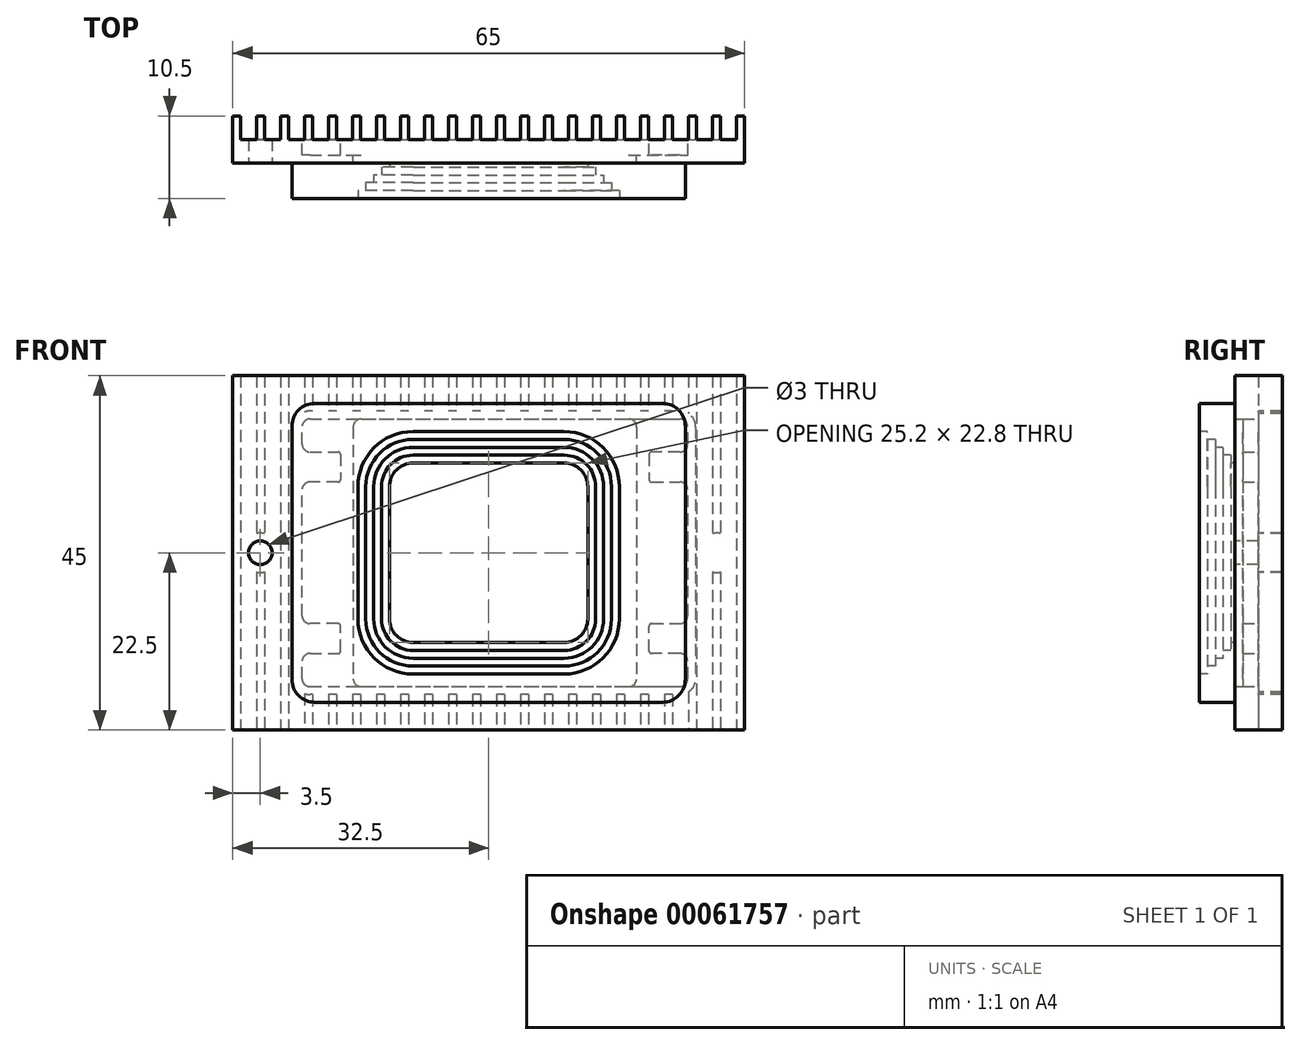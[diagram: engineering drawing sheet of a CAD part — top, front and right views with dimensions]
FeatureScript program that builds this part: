
annotation { "Feature Type Name" : "Feature", "Feature Type Description" : "" }
export const myFeature = defineFeature(function(context is Context, id is Id, definition is map)
    precondition{}
    {
        {
            var Q0;
            Q0=qCreatedBy(makeId("Front.planeOp"),FACE);
            var sketch = newSketch(context, id + "F0", { "sketchPlane" : qUnion([Q0])});
            skLineSegment(sketch, "E0.bottom", {"start": v(-32.5, 22.5) * mm, "end": v(32.5, 22.5) * mm});
            skLineSegment(sketch, "E0.top", {"start": v(-32.5, -22.5) * mm, "end": v(32.5, -22.5) * mm});
            skLineSegment(sketch, "E0.left", {"start": v(-32.5, 22.5) * mm, "end": v(-32.5, -22.5) * mm});
            skLineSegment(sketch, "E0.right", {"start": v(32.5, 22.5) * mm, "end": v(32.5, -22.5) * mm});
            skPoint(sketch, "E1.visualSharp", {"position": v(-32.5, 22.5) * mm});
            skLineSegment(sketch, "E1.filletArc", {"start": v(-32.5, 22.5) * mm, "end": v(-32.5, 22.5) * mm});
            skPoint(sketch, "E2.visualSharp", {"position": v(32.5, 22.5) * mm});
            skLineSegment(sketch, "E2.filletArc", {"start": v(32.5, 22.5) * mm, "end": v(32.5, 22.5) * mm});
            skPoint(sketch, "E3.visualSharp", {"position": v(32.5, -22.5) * mm});
            skLineSegment(sketch, "E3.filletArc", {"start": v(32.5, -22.5) * mm, "end": v(32.5, -22.5) * mm});
            skPoint(sketch, "E4.visualSharp", {"position": v(-32.5, -22.5) * mm});
            skLineSegment(sketch, "E4.filletArc", {"start": v(-32.5, -22.5) * mm, "end": v(-32.5, -22.5) * mm});
            skPoint(sketch, "E5", {"position": v(0, 22.5) * mm});
            skPoint(sketch, "E6", {"position": v(32.5, 0) * mm});
            skSolve(sketch);
        }
        {
            var Q0;
            Q0=makeQuery(id+"F0.imprint","IMPRINT",FACE,{"disambiguationData":[TD([[makeQuery(id+"F0.imprint","IMPRINT",EDGE,{"derivedFrom":sQuery(id+"F0.wireOp",EDGE,"E0.bottom")}),-1.0]])]});
            var Q1;
            Q1=makeQuery(id+"F0.imprint","IMPRINT",FACE,{"disambiguationData":[TD([[makeQuery(id+"F0.imprint","IMPRINT",EDGE,{"derivedFrom":sQuery(id+"F0.wireOp",EDGE,"E0.bottom")}),-1.0]])]});
            extrude(context, id + "F1", {"entities" : qUnion([Q0, Q1]), "depth" : 3 * mm});
        }
        {
            var Q0;
            Q0=makeQuery(id+"F1.opExtrude","CAP_FACE",FACE,{"disambiguationData":[OSD([sQuery(id+"F0.wireOp",EDGE,"E0.bottom"),sQuery(id+"F0.wireOp",EDGE,"E0.top"),sQuery(id+"F0.wireOp",EDGE,"E0.left"),sQuery(id+"F0.wireOp",EDGE,"E0.right"),sQuery(id+"F0.wireOp",EDGE,"E1.filletArc"),sQuery(id+"F0.wireOp",EDGE,"E2.filletArc"),sQuery(id+"F0.wireOp",EDGE,"E3.filletArc"),sQuery(id+"F0.wireOp",EDGE,"E4.filletArc")])],"isStart":false});
            var sketch = newSketch(context, id + "F2", { "sketchPlane" : qUnion([Q0])});
            skLineSegment(sketch, "E7.bottom", {"start": v(-22.09, 18.99) * mm, "end": v(22.09, 18.99) * mm});
            skLineSegment(sketch, "E7.top", {"start": v(-22.09, -18.99) * mm, "end": v(22.09, -18.99) * mm});
            skLineSegment(sketch, "E7.left", {"start": v(-24.98, 16.09) * mm, "end": v(-24.98, -16.09) * mm});
            skLineSegment(sketch, "E7.right", {"start": v(24.98, 16.09) * mm, "end": v(24.98, -16.09) * mm});
            skPoint(sketch, "E8", {"position": v(0, 18.99) * mm});
            skPoint(sketch, "E9", {"position": v(24.98, 0) * mm});
            skPoint(sketch, "E10.visualSharp", {"position": v(-24.98, 18.99) * mm});
            skArc(sketch, "E10.filletArc", {"start": v(-22.09, 18.99) * mm, "mid": v(-24.14, 18.14) * mm, "end": v(-24.98, 16.09) * mm});
            skPoint(sketch, "E11.visualSharp", {"position": v(24.99, -18.98) * mm});
            skArc(sketch, "E11.filletArc", {"start": v(22.09, -18.99) * mm, "mid": v(24.14, -18.14) * mm, "end": v(24.98, -16.09) * mm});
            skPoint(sketch, "E12.visualSharp", {"position": v(24.99, 18.98) * mm});
            skArc(sketch, "E12.filletArc", {"start": v(24.98, 16.09) * mm, "mid": v(24.14, 18.14) * mm, "end": v(22.09, 18.99) * mm});
            skPoint(sketch, "E13.visualSharp", {"position": v(-24.98, -18.99) * mm});
            skArc(sketch, "E13.filletArc", {"start": v(-24.98, -16.09) * mm, "mid": v(-24.14, -18.14) * mm, "end": v(-22.09, -18.99) * mm});
            skSolve(sketch);
        }
        {
            var Q0;
            Q0=makeQuery(id+"F2.imprint","IMPRINT",FACE,{"disambiguationData":[TD([[makeQuery(id+"F2.imprint","IMPRINT",EDGE,{"derivedFrom":sQuery(id+"F2.wireOp",EDGE,"E7.bottom")}),-1.0]])]});
            extrude(context, id + "F3", {"entities" : qUnion([Q0]), "operationType" : NewBodyOperationType.ADD, "depth" : 4.5 * mm});
        }
        {
            var Q0;
            Q0=makeQuery(id+"F3.opExtrude","CAP_FACE",FACE,{"disambiguationData":[OSD([sQuery(id+"F2.wireOp",EDGE,"E7.bottom"),sQuery(id+"F2.wireOp",EDGE,"E7.top"),sQuery(id+"F2.wireOp",EDGE,"E7.left"),sQuery(id+"F2.wireOp",EDGE,"E7.right"),sQuery(id+"F2.wireOp",EDGE,"E10.filletArc"),sQuery(id+"F2.wireOp",EDGE,"E11.filletArc"),sQuery(id+"F2.wireOp",EDGE,"E12.filletArc"),sQuery(id+"F2.wireOp",EDGE,"E13.filletArc")])],"isStart":false});
            var sketch = newSketch(context, id + "F4", { "sketchPlane" : qUnion([Q0])});
            skLineSegment(sketch, "E14.bottom", {"start": v(-9.6, 11.4) * mm, "end": v(9.6, 11.4) * mm});
            skLineSegment(sketch, "E14.top", {"start": v(-9.6, -11.4) * mm, "end": v(9.6, -11.4) * mm});
            skLineSegment(sketch, "E14.left", {"start": v(-12.6, 8.4) * mm, "end": v(-12.6, -8.4) * mm});
            skLineSegment(sketch, "E14.right", {"start": v(12.6, 8.4) * mm, "end": v(12.6, -8.4) * mm});
            skPoint(sketch, "E15", {"position": v(0, 11.4) * mm});
            skPoint(sketch, "E16", {"position": v(12.6, 0) * mm});
            skPoint(sketch, "E17.visualSharp", {"position": v(-12.6, 11.4) * mm});
            skArc(sketch, "E17.filletArc", {"start": v(-9.6, 11.4) * mm, "mid": v(-11.72, 10.52) * mm, "end": v(-12.6, 8.4) * mm});
            skPoint(sketch, "E18.visualSharp", {"position": v(12.6, 11.4) * mm});
            skArc(sketch, "E18.filletArc", {"start": v(12.6, 8.4) * mm, "mid": v(11.72, 10.52) * mm, "end": v(9.6, 11.4) * mm});
            skPoint(sketch, "E19.visualSharp", {"position": v(12.6, -11.4) * mm});
            skArc(sketch, "E19.filletArc", {"start": v(9.6, -11.4) * mm, "mid": v(11.72, -10.52) * mm, "end": v(12.6, -8.4) * mm});
            skPoint(sketch, "E20.visualSharp", {"position": v(-12.6, -11.4) * mm});
            skArc(sketch, "E20.filletArc", {"start": v(-12.6, -8.4) * mm, "mid": v(-11.72, -10.52) * mm, "end": v(-9.6, -11.4) * mm});
            skCircle(sketch, "E21", {"center": v(-29, 0) * mm, "radius": 1.5 * mm});
            skCircle(sketch, "E22.MirrorC", {"center": v(29, 0) * mm, "radius": 1.5 * mm});
            skSolve(sketch);
        }
        {
            var Q0;
            Q0=makeQuery(id+"F4.imprint","IMPRINT",FACE,{"disambiguationData":[TD([[makeQuery(id+"F4.imprint","IMPRINT",EDGE,{"derivedFrom":sQuery(id+"F4.wireOp",EDGE,"E14.bottom")}),-1.0]])]});
            var Q1;
            Q1=makeQuery(id+"F4.imprint","IMPRINT",FACE,{"disambiguationData":[TD([[makeQuery(id+"F4.imprint","IMPRINT",EDGE,{"derivedFrom":sQuery(id+"F4.wireOp",EDGE,"E21")}),1.0]])]});
            var Q2;
            Q2=makeQuery(id+"F4.imprint","IMPRINT",FACE,{"disambiguationData":[TD([[makeQuery(id+"F4.imprint","IMPRINT",EDGE,{"derivedFrom":sQuery(id+"F4.wireOp",EDGE,"E22.MirrorC")}),-1.0]])]});
            extrude(context, id + "F5", {"entities" : qUnion([Q0, Q1, Q2]), "operationType" : NewBodyOperationType.REMOVE, "oppositeDirection" : true, "depth" : 25 * mm});
        }
        {
            var Q0;
            Q0=makeQuery(id+"F1.opExtrude","CAP_FACE",FACE,{"disambiguationData":[OSD([sQuery(id+"F0.wireOp",EDGE,"E0.bottom"),sQuery(id+"F0.wireOp",EDGE,"E0.top"),sQuery(id+"F0.wireOp",EDGE,"E0.left"),sQuery(id+"F0.wireOp",EDGE,"E0.right")])],"isStart":true});
            var sketch = newSketch(context, id + "F6", { "sketchPlane" : qUnion([Q0])});
            skPoint(sketch, "E23", {"position": v(-32.5, 0) * mm});
            skPoint(sketch, "E23.positionSnap0", {"position": v(-25.3, 0) * mm});
            skLineSegment(sketch, "E24", {"start": v(-24.3, -12.8) * mm, "end": v(-20.7, -12.8) * mm});
            skLineSegment(sketch, "E25", {"start": v(-20.4, -12.5) * mm, "end": v(-20.4, -9.3) * mm});
            skLineSegment(sketch, "E26", {"start": v(-20.7, -9) * mm, "end": v(-24.3, -9) * mm});
            skLineSegment(sketch, "E27", {"start": v(-24.3, 12.8) * mm, "end": v(-20.7, 12.8) * mm});
            skLineSegment(sketch, "E28", {"start": v(-20.4, 12.5) * mm, "end": v(-20.4, 9.3) * mm});
            skLineSegment(sketch, "E29", {"start": v(-20.7, 9) * mm, "end": v(-24.3, 9) * mm});
            skLineSegment(sketch, "E30", {"start": v(-0.8, 17) * mm, "end": v(-0.8, -17) * mm, "construction": true});
            skLineSegment(sketch, "E31", {"start": v(-25.3, -16) * mm, "end": v(-25.3, -13.8) * mm});
            skLineSegment(sketch, "E32", {"start": v(-25.3, -8) * mm, "end": v(-25.3, 8) * mm});
            skLineSegment(sketch, "E33", {"start": v(-25.3, 13.8) * mm, "end": v(-25.3, 16) * mm});
            skPoint(sketch, "E34.visualSharp", {"position": v(-25.3, 12.8) * mm});
            skArc(sketch, "E34.filletArc", {"start": v(-25.3, 13.8) * mm, "mid": v(-25, 13.1) * mm, "end": v(-24.3, 12.8) * mm});
            skPoint(sketch, "E35.visualSharp", {"position": v(-25.3, 17.24) * mm});
            skArc(sketch, "E35.filletArc", {"start": v(-24.3, 17) * mm, "mid": v(-25, 16.7) * mm, "end": v(-25.3, 16) * mm});
            skPoint(sketch, "E36.visualSharp", {"position": v(-25.3, -9) * mm});
            skArc(sketch, "E36.filletArc", {"start": v(-25.3, -8) * mm, "mid": v(-25, -8.7) * mm, "end": v(-24.3, -9) * mm});
            skPoint(sketch, "E37.visualSharp", {"position": v(-25.3, -17.23) * mm});
            skArc(sketch, "E37.filletArc", {"start": v(-25.3, -16) * mm, "mid": v(-25, -16.7) * mm, "end": v(-24.3, -17) * mm});
            skPoint(sketch, "E38.visualSharp", {"position": v(-20.4, 9) * mm});
            skArc(sketch, "E38.filletArc", {"start": v(-20.7, 9) * mm, "mid": v(-20.49, 9.09) * mm, "end": v(-20.4, 9.3) * mm});
            skPoint(sketch, "E39.visualSharp", {"position": v(-20.4, 12.8) * mm});
            skArc(sketch, "E39.filletArc", {"start": v(-20.4, 12.5) * mm, "mid": v(-20.49, 12.71) * mm, "end": v(-20.7, 12.8) * mm});
            skPoint(sketch, "E40.visualSharp", {"position": v(-20.4, -9) * mm});
            skArc(sketch, "E40.filletArc", {"start": v(-20.4, -9.3) * mm, "mid": v(-20.49, -9.09) * mm, "end": v(-20.7, -9) * mm});
            skPoint(sketch, "E41.visualSharp", {"position": v(-20.4, -12.8) * mm});
            skArc(sketch, "E41.filletArc", {"start": v(-20.7, -12.8) * mm, "mid": v(-20.49, -12.71) * mm, "end": v(-20.4, -12.5) * mm});
            skPoint(sketch, "E42.visualSharp", {"position": v(-25.3, 9) * mm});
            skArc(sketch, "E42.filletArc", {"start": v(-24.3, 9) * mm, "mid": v(-25, 8.7) * mm, "end": v(-25.3, 8) * mm});
            skPoint(sketch, "E43.visualSharp", {"position": v(-25.3, -12.8) * mm});
            skArc(sketch, "E43.filletArc", {"start": v(-24.3, -12.8) * mm, "mid": v(-25, -13.1) * mm, "end": v(-25.3, -13.8) * mm});
            skArc(sketch, "E44.MirrorCS", {"start": v(23.7, -16) * mm, "mid": v(23.4, -16.7) * mm, "end": v(22.7, -17) * mm});
            skArc(sketch, "E45.MirrorCS", {"start": v(22.7, -12.8) * mm, "mid": v(23.4, -13.1) * mm, "end": v(23.7, -13.8) * mm});
            skLineSegment(sketch, "E46.MirrorCS", {"start": v(22.7, -12.8) * mm, "end": v(19.1, -12.8) * mm});
            skArc(sketch, "E47.MirrorCS", {"start": v(19.1, -12.8) * mm, "mid": v(18.89, -12.71) * mm, "end": v(18.8, -12.5) * mm});
            skLineSegment(sketch, "E48.MirrorCS", {"start": v(18.8, -12.5) * mm, "end": v(18.8, -9.3) * mm});
            skArc(sketch, "E49.MirrorCS", {"start": v(18.8, -9.3) * mm, "mid": v(18.89, -9.09) * mm, "end": v(19.1, -9) * mm});
            skLineSegment(sketch, "E50.MirrorCS", {"start": v(19.1, -9) * mm, "end": v(22.7, -9) * mm});
            skArc(sketch, "E51.MirrorCS", {"start": v(23.7, -8) * mm, "mid": v(23.4, -8.7) * mm, "end": v(22.7, -9) * mm});
            skLineSegment(sketch, "E52.MirrorCS", {"start": v(23.7, -8) * mm, "end": v(23.7, 8) * mm});
            skArc(sketch, "E53.MirrorCS", {"start": v(22.7, 9) * mm, "mid": v(23.4, 8.7) * mm, "end": v(23.7, 8) * mm});
            skLineSegment(sketch, "E54.MirrorCS", {"start": v(19.1, 9) * mm, "end": v(22.7, 9) * mm});
            skArc(sketch, "E55.MirrorCS", {"start": v(19.1, 9) * mm, "mid": v(18.89, 9.09) * mm, "end": v(18.8, 9.3) * mm});
            skLineSegment(sketch, "E56.MirrorCS", {"start": v(18.8, 12.5) * mm, "end": v(18.8, 9.3) * mm});
            skArc(sketch, "E57.MirrorCS", {"start": v(18.8, 12.5) * mm, "mid": v(18.89, 12.71) * mm, "end": v(19.1, 12.8) * mm});
            skLineSegment(sketch, "E58.MirrorCS", {"start": v(22.7, 12.8) * mm, "end": v(19.1, 12.8) * mm});
            skArc(sketch, "E59.MirrorCS", {"start": v(23.7, 13.8) * mm, "mid": v(23.4, 13.1) * mm, "end": v(22.7, 12.8) * mm});
            skLineSegment(sketch, "E60.MirrorCS", {"start": v(23.7, 13.8) * mm, "end": v(23.7, 16) * mm});
            skArc(sketch, "E61.MirrorCS", {"start": v(22.7, 17) * mm, "mid": v(23.4, 16.7) * mm, "end": v(23.7, 16) * mm});
            skLineSegment(sketch, "E62", {"start": v(22.7, -17) * mm, "end": v(-24.3, -17) * mm});
            skLineSegment(sketch, "E63", {"start": v(22.7, 17) * mm, "end": v(-24.3, 17) * mm});
            skLineSegment(sketch, "E64", {"start": v(-25.3, 0) * mm, "end": v(23.7, 0) * mm, "construction": true});
            skLineSegment(sketch, "E65.MirrorCS", {"start": v(23.7, -16) * mm, "end": v(23.7, -13.8) * mm});
            skLineSegment(sketch, "E66.bottom", {"start": v(-24.3, 16.9) * mm, "end": v(22.7, 16.9) * mm, "construction": true});
            skLineSegment(sketch, "E66.top", {"start": v(-24.3, -16.9) * mm, "end": v(22.7, -16.9) * mm, "construction": true});
            skLineSegment(sketch, "E66.left", {"start": v(-24.3, 16.9) * mm, "end": v(-24.3, -16.9) * mm, "construction": true});
            skLineSegment(sketch, "E66.right", {"start": v(22.7, 16.9) * mm, "end": v(22.7, -16.9) * mm, "construction": true});
            skLineSegment(sketch, "E67", {"start": v(-24.3, -16.9) * mm, "end": v(22.7, 16.9) * mm, "construction": true});
            skLineSegment(sketch, "E68", {"start": v(22.7, -16.9) * mm, "end": v(-24.3, 16.9) * mm, "construction": true});
            skPoint(sketch, "E69", {"position": v(-0.8, 0) * mm});
            skLineSegment(sketch, "E70.bottom", {"start": v(22.7, 12.9) * mm, "end": v(18.7, 12.9) * mm, "construction": true});
            skLineSegment(sketch, "E70.top", {"start": v(22.7, 8.9) * mm, "end": v(18.7, 8.9) * mm, "construction": true});
            skLineSegment(sketch, "E70.left", {"start": v(22.7, 12.9) * mm, "end": v(22.7, 8.9) * mm, "construction": true});
            skLineSegment(sketch, "E70.right", {"start": v(18.7, 12.9) * mm, "end": v(18.7, 8.9) * mm, "construction": true});
            skSolve(sketch);
        }
        {
            var Q0;
            Q0=makeQuery(id+"F6.imprint","IMPRINT",FACE,{"disambiguationData":[TD([[makeQuery(id+"F6.imprint","IMPRINT",EDGE,{"derivedFrom":sQuery(id+"F6.wireOp",EDGE,"E24")}),-1.0]])]});
            extrude(context, id + "F7", {"entities" : qUnion([Q0]), "operationType" : NewBodyOperationType.REMOVE, "oppositeDirection" : true, "depth" : 2 * mm});
        }
        {
            var Q0;
            Q0=makeQuery(id+"F3.opExtrude","CAP_FACE",FACE,{"disambiguationData":[OSD([sQuery(id+"F2.wireOp",EDGE,"E7.bottom"),sQuery(id+"F2.wireOp",EDGE,"E7.top"),sQuery(id+"F2.wireOp",EDGE,"E7.left"),sQuery(id+"F2.wireOp",EDGE,"E7.right"),sQuery(id+"F2.wireOp",EDGE,"E10.filletArc"),sQuery(id+"F2.wireOp",EDGE,"E11.filletArc"),sQuery(id+"F2.wireOp",EDGE,"E12.filletArc"),sQuery(id+"F2.wireOp",EDGE,"E13.filletArc")])],"isStart":false});
            var sketch = newSketch(context, id + "F8", { "sketchPlane" : qUnion([Q0])});
            skLineSegment(sketch, "E71.0", {"start": v(-9.6, 12.4) * mm, "end": v(9.6, 12.4) * mm});
            skArc(sketch, "E71.1", {"start": v(13.6, 8.4) * mm, "mid": v(12.43, 11.23) * mm, "end": v(9.6, 12.4) * mm});
            skArc(sketch, "E71.2", {"start": v(-9.6, 12.4) * mm, "mid": v(-12.43, 11.23) * mm, "end": v(-13.6, 8.4) * mm});
            skLineSegment(sketch, "E71.3", {"start": v(13.6, 8.4) * mm, "end": v(13.6, -8.4) * mm});
            skLineSegment(sketch, "E71.4", {"start": v(-13.6, 8.4) * mm, "end": v(-13.6, -8.4) * mm});
            skArc(sketch, "E71.5", {"start": v(-13.6, -8.4) * mm, "mid": v(-12.43, -11.23) * mm, "end": v(-9.6, -12.4) * mm});
            skLineSegment(sketch, "E71.6", {"start": v(-9.6, -12.4) * mm, "end": v(9.6, -12.4) * mm});
            skArc(sketch, "E71.7", {"start": v(9.6, -12.4) * mm, "mid": v(12.43, -11.23) * mm, "end": v(13.6, -8.4) * mm});
            skSolve(sketch);
        }
        {
            var Q0;
            Q0=makeQuery(id+"F8.imprint","IMPRINT",FACE,{"disambiguationData":[TD([[makeQuery(id+"F8.imprint","IMPRINT",EDGE,{"derivedFrom":sQuery(id+"F8.wireOp",EDGE,"E71.0")}),-1.0]])]});
            extrude(context, id + "F9", {"entities" : qUnion([Q0]), "operationType" : NewBodyOperationType.REMOVE, "oppositeDirection" : true, "depth" : 4 * mm});
        }
        {
            var Q0;
            Q0=makeQuery(id+"F3.opExtrude","CAP_FACE",FACE,{"disambiguationData":[OSD([sQuery(id+"F2.wireOp",EDGE,"E7.bottom"),sQuery(id+"F2.wireOp",EDGE,"E7.top"),sQuery(id+"F2.wireOp",EDGE,"E7.left"),sQuery(id+"F2.wireOp",EDGE,"E7.right"),sQuery(id+"F2.wireOp",EDGE,"E10.filletArc"),sQuery(id+"F2.wireOp",EDGE,"E11.filletArc"),sQuery(id+"F2.wireOp",EDGE,"E12.filletArc"),sQuery(id+"F2.wireOp",EDGE,"E13.filletArc")])],"isStart":false});
            var sketch = newSketch(context, id + "F10", { "sketchPlane" : qUnion([Q0])});
            skLineSegment(sketch, "E72.0", {"start": v(-9.6, 13.4) * mm, "end": v(9.6, 13.4) * mm});
            skArc(sketch, "E72.1", {"start": v(14.6, 8.4) * mm, "mid": v(13.14, 11.94) * mm, "end": v(9.6, 13.4) * mm});
            skArc(sketch, "E72.2", {"start": v(-9.6, 13.4) * mm, "mid": v(-13.14, 11.94) * mm, "end": v(-14.6, 8.4) * mm});
            skLineSegment(sketch, "E72.3", {"start": v(14.6, 8.4) * mm, "end": v(14.6, -8.4) * mm});
            skLineSegment(sketch, "E72.4", {"start": v(-14.6, 8.4) * mm, "end": v(-14.6, -8.4) * mm});
            skArc(sketch, "E72.5", {"start": v(-14.6, -8.4) * mm, "mid": v(-13.14, -11.94) * mm, "end": v(-9.6, -13.4) * mm});
            skLineSegment(sketch, "E72.6", {"start": v(-9.6, -13.4) * mm, "end": v(9.6, -13.4) * mm});
            skArc(sketch, "E72.7", {"start": v(9.6, -13.4) * mm, "mid": v(13.14, -11.94) * mm, "end": v(14.6, -8.4) * mm});
            skLineSegment(sketch, "E73.0", {"start": v(19.98, 13.99) * mm, "end": v(-19.98, 13.99) * mm});
            skLineSegment(sketch, "E73.1", {"start": v(19.98, -13.99) * mm, "end": v(19.98, 13.99) * mm});
            skLineSegment(sketch, "E73.2", {"start": v(-19.98, -13.99) * mm, "end": v(19.98, -13.99) * mm});
            skLineSegment(sketch, "E73.3", {"start": v(-19.98, 13.99) * mm, "end": v(-19.98, -13.99) * mm});
            skSolve(sketch);
        }
        {
            var Q0;
            Q0=makeQuery(id+"F10.imprint","IMPRINT",FACE,{"disambiguationData":[TD([[makeQuery(id+"F10.imprint","IMPRINT",EDGE,{"derivedFrom":sQuery(id+"F10.wireOp",EDGE,"E72.0")}),-1.0]])]});
            extrude(context, id + "F11", {"entities" : qUnion([Q0]), "operationType" : NewBodyOperationType.REMOVE, "oppositeDirection" : true, "depth" : 3 * mm});
        }
        {
            var Q0;
            Q0=makeQuery(id+"F3.opExtrude","CAP_FACE",FACE,{"disambiguationData":[OSD([sQuery(id+"F2.wireOp",EDGE,"E7.bottom"),sQuery(id+"F2.wireOp",EDGE,"E7.top"),sQuery(id+"F2.wireOp",EDGE,"E7.left"),sQuery(id+"F2.wireOp",EDGE,"E7.right"),sQuery(id+"F2.wireOp",EDGE,"E10.filletArc"),sQuery(id+"F2.wireOp",EDGE,"E11.filletArc"),sQuery(id+"F2.wireOp",EDGE,"E12.filletArc"),sQuery(id+"F2.wireOp",EDGE,"E13.filletArc")])],"isStart":false});
            var sketch = newSketch(context, id + "F12", { "sketchPlane" : qUnion([Q0])});
            skLineSegment(sketch, "E74.0", {"start": v(-9.6, 14.4) * mm, "end": v(9.6, 14.4) * mm});
            skArc(sketch, "E74.1", {"start": v(15.6, 8.4) * mm, "mid": v(13.84, 12.64) * mm, "end": v(9.6, 14.4) * mm});
            skArc(sketch, "E74.2", {"start": v(-9.6, 14.4) * mm, "mid": v(-13.84, 12.64) * mm, "end": v(-15.6, 8.4) * mm});
            skLineSegment(sketch, "E74.3", {"start": v(15.6, 8.4) * mm, "end": v(15.6, -8.4) * mm});
            skLineSegment(sketch, "E74.4", {"start": v(-15.6, 8.4) * mm, "end": v(-15.6, -8.4) * mm});
            skArc(sketch, "E74.5", {"start": v(-15.6, -8.4) * mm, "mid": v(-13.84, -12.64) * mm, "end": v(-9.6, -14.4) * mm});
            skLineSegment(sketch, "E74.6", {"start": v(-9.6, -14.4) * mm, "end": v(9.6, -14.4) * mm});
            skArc(sketch, "E74.7", {"start": v(9.6, -14.4) * mm, "mid": v(13.84, -12.64) * mm, "end": v(15.6, -8.4) * mm});
            skSolve(sketch);
        }
        {
            var Q0;
            Q0=makeQuery(id+"F12.imprint","IMPRINT",FACE,{"disambiguationData":[TD([[makeQuery(id+"F12.imprint","IMPRINT",EDGE,{"derivedFrom":sQuery(id+"F12.wireOp",EDGE,"E74.0")}),-1.0]])]});
            extrude(context, id + "F13", {"entities" : qUnion([Q0]), "operationType" : NewBodyOperationType.REMOVE, "oppositeDirection" : true, "depth" : 2 * mm});
        }
        {
            var Q0;
            Q0=makeQuery(id+"F3.opExtrude","CAP_FACE",FACE,{"disambiguationData":[OSD([sQuery(id+"F2.wireOp",EDGE,"E7.bottom"),sQuery(id+"F2.wireOp",EDGE,"E7.top"),sQuery(id+"F2.wireOp",EDGE,"E7.left"),sQuery(id+"F2.wireOp",EDGE,"E7.right"),sQuery(id+"F2.wireOp",EDGE,"E10.filletArc"),sQuery(id+"F2.wireOp",EDGE,"E11.filletArc"),sQuery(id+"F2.wireOp",EDGE,"E12.filletArc"),sQuery(id+"F2.wireOp",EDGE,"E13.filletArc")])],"isStart":false});
            var sketch = newSketch(context, id + "F14", { "sketchPlane" : qUnion([Q0])});
            skLineSegment(sketch, "E75.0", {"start": v(-9.6, 15.4) * mm, "end": v(9.6, 15.4) * mm});
            skArc(sketch, "E75.1", {"start": v(16.6, 8.4) * mm, "mid": v(14.55, 13.35) * mm, "end": v(9.6, 15.4) * mm});
            skArc(sketch, "E75.2", {"start": v(-9.6, 15.4) * mm, "mid": v(-14.55, 13.35) * mm, "end": v(-16.6, 8.4) * mm});
            skLineSegment(sketch, "E75.3", {"start": v(16.6, 8.4) * mm, "end": v(16.6, -8.4) * mm});
            skLineSegment(sketch, "E75.4", {"start": v(-16.6, 8.4) * mm, "end": v(-16.6, -8.4) * mm});
            skArc(sketch, "E75.5", {"start": v(-16.6, -8.4) * mm, "mid": v(-14.55, -13.35) * mm, "end": v(-9.6, -15.4) * mm});
            skLineSegment(sketch, "E75.6", {"start": v(-9.6, -15.4) * mm, "end": v(9.6, -15.4) * mm});
            skArc(sketch, "E75.7", {"start": v(9.6, -15.4) * mm, "mid": v(14.55, -13.35) * mm, "end": v(16.6, -8.4) * mm});
            skLineSegment(sketch, "E76.0", {"start": v(19.98, 13.99) * mm, "end": v(-19.98, 13.99) * mm});
            skLineSegment(sketch, "E76.1", {"start": v(19.98, -13.99) * mm, "end": v(19.98, 13.99) * mm});
            skLineSegment(sketch, "E76.2", {"start": v(-19.98, -13.99) * mm, "end": v(19.98, -13.99) * mm});
            skLineSegment(sketch, "E76.3", {"start": v(-19.98, 13.99) * mm, "end": v(-19.98, -13.99) * mm});
            skSolve(sketch);
        }
        {
            var Q0;
            {var subQ5=makeQuery(id+"F13.boolean.opBoolean","COPY",EDGE,{"derivedFrom":makeQuery(id+"F13.opExtrude","CAP_EDGE",EDGE,{"disambiguationData":[OSD([sQuery(id+"F12.wireOp",EDGE,"E74.0")])],"isStart":true})});Q0=makeQuery(id+"F14.imprint","IMPRINT",FACE,{"disambiguationData":[TD([[makeQuery(id+"F14.imprint","IMPRINT",EDGE,{"derivedFrom":subQ5}),-1.0]])]});}
            var Q1;
            {var subQ5=makeQuery(id+"F13.boolean.opBoolean","COPY",EDGE,{"derivedFrom":makeQuery(id+"F13.opExtrude","CAP_EDGE",EDGE,{"disambiguationData":[OSD([sQuery(id+"F12.wireOp",EDGE,"E74.6")])],"isStart":true})});Q1=makeQuery(id+"F14.imprint","IMPRINT",FACE,{"disambiguationData":[TD([[makeQuery(id+"F14.imprint","IMPRINT",EDGE,{"derivedFrom":subQ5}),1.0]])]});}
            var Q2;
            {var subQ6=sQuery(id+"F14.wireOp",EDGE,"E75.0");Q2=makeQuery(id+"F14.imprint","IMPRINT",FACE,{"disambiguationData":[TD([[makeQuery(id+"F14.imprint","IMPRINT",EDGE,{"derivedFrom":subQ6}),-1.0]])]});}
            var Q3;
            {var subQ9=sQuery(id+"F14.wireOp",EDGE,"E75.3");Q3=makeQuery(id+"F14.imprint","IMPRINT",FACE,{"disambiguationData":[TD([[makeQuery(id+"F14.imprint","IMPRINT",EDGE,{"derivedFrom":subQ9}),-1.0]])]});}
            var Q4;
            {var subQ6=sQuery(id+"F14.wireOp",EDGE,"E75.4");Q4=makeQuery(id+"F14.imprint","IMPRINT",FACE,{"disambiguationData":[TD([[makeQuery(id+"F14.imprint","IMPRINT",EDGE,{"derivedFrom":subQ6}),1.0]])]});}
            var Q5;
            {var subQ6=sQuery(id+"F14.wireOp",EDGE,"E75.6");Q5=makeQuery(id+"F14.imprint","IMPRINT",FACE,{"disambiguationData":[TD([[makeQuery(id+"F14.imprint","IMPRINT",EDGE,{"derivedFrom":subQ6}),1.0]])]});}
            var Q6;
            {var subQ0=makeQuery(id+"F13.boolean.opBoolean","COPY",EDGE,{"derivedFrom":makeQuery(id+"F13.opExtrude","CAP_EDGE",EDGE,{"disambiguationData":[OSD([sQuery(id+"F12.wireOp",EDGE,"E74.3")])],"isStart":true})});Q6=makeQuery(id+"F14.imprint","IMPRINT",FACE,{"disambiguationData":[TD([[makeQuery(id+"F14.imprint","IMPRINT",EDGE,{"derivedFrom":subQ0}),-1.0]])]});}
            extrude(context, id + "F15", {"entities" : qUnion([Q0, Q1, Q2, Q3, Q4, Q5, Q6]), "operationType" : NewBodyOperationType.REMOVE, "oppositeDirection" : true, "depth" : 1 * mm});
        }
        {
            var Q0;
            Q0=makeQuery(id+"F7.boolean.opBoolean","COPY",FACE,{"derivedFrom":makeQuery(id+"F7.opExtrude","CAP_FACE",FACE,{"disambiguationData":[OSD([sQuery(id+"F0.wireOp",EDGE,"E0.bottom"),sQuery(id+"F0.wireOp",EDGE,"E0.top"),sQuery(id+"F0.wireOp",EDGE,"E0.left"),sQuery(id+"F0.wireOp",EDGE,"E0.right"),sQuery(id+"F4.wireOp",EDGE,"E14.bottom"),sQuery(id+"F4.wireOp",EDGE,"E14.top"),sQuery(id+"F4.wireOp",EDGE,"E14.left"),sQuery(id+"F4.wireOp",EDGE,"E14.right"),sQuery(id+"F4.wireOp",EDGE,"E17.filletArc"),sQuery(id+"F4.wireOp",EDGE,"E18.filletArc"),sQuery(id+"F4.wireOp",EDGE,"E19.filletArc"),sQuery(id+"F4.wireOp",EDGE,"E20.filletArc"),sQuery(id+"F6.wireOp",EDGE,"E24"),sQuery(id+"F6.wireOp",EDGE,"E25"),sQuery(id+"F6.wireOp",EDGE,"E26"),sQuery(id+"F6.wireOp",EDGE,"E27"),sQuery(id+"F6.wireOp",EDGE,"E28"),sQuery(id+"F6.wireOp",EDGE,"E29"),sQuery(id+"F6.wireOp",EDGE,"E31"),sQuery(id+"F6.wireOp",EDGE,"E32"),sQuery(id+"F6.wireOp",EDGE,"E33"),sQuery(id+"F6.wireOp",EDGE,"E34.filletArc"),sQuery(id+"F6.wireOp",EDGE,"E35.filletArc"),sQuery(id+"F6.wireOp",EDGE,"E36.filletArc"),sQuery(id+"F6.wireOp",EDGE,"E37.filletArc"),sQuery(id+"F6.wireOp",EDGE,"E38.filletArc"),sQuery(id+"F6.wireOp",EDGE,"E39.filletArc"),sQuery(id+"F6.wireOp",EDGE,"E40.filletArc"),sQuery(id+"F6.wireOp",EDGE,"E41.filletArc"),sQuery(id+"F6.wireOp",EDGE,"E42.filletArc"),sQuery(id+"F6.wireOp",EDGE,"E43.filletArc"),sQuery(id+"F6.wireOp",EDGE,"E44.MirrorCS"),sQuery(id+"F6.wireOp",EDGE,"E45.MirrorCS"),sQuery(id+"F6.wireOp",EDGE,"E46.MirrorCS"),sQuery(id+"F6.wireOp",EDGE,"E47.MirrorCS"),sQuery(id+"F6.wireOp",EDGE,"E48.MirrorCS"),sQuery(id+"F6.wireOp",EDGE,"E49.MirrorCS"),sQuery(id+"F6.wireOp",EDGE,"E50.MirrorCS"),sQuery(id+"F6.wireOp",EDGE,"E51.MirrorCS"),sQuery(id+"F6.wireOp",EDGE,"E52.MirrorCS"),sQuery(id+"F6.wireOp",EDGE,"E53.MirrorCS"),sQuery(id+"F6.wireOp",EDGE,"E54.MirrorCS"),sQuery(id+"F6.wireOp",EDGE,"E55.MirrorCS"),sQuery(id+"F6.wireOp",EDGE,"E56.MirrorCS"),sQuery(id+"F6.wireOp",EDGE,"E57.MirrorCS"),sQuery(id+"F6.wireOp",EDGE,"E58.MirrorCS"),sQuery(id+"F6.wireOp",EDGE,"E59.MirrorCS"),sQuery(id+"F6.wireOp",EDGE,"E60.MirrorCS"),sQuery(id+"F6.wireOp",EDGE,"E61.MirrorCS"),sQuery(id+"F6.wireOp",EDGE,"E62"),sQuery(id+"F6.wireOp",EDGE,"E63"),sQuery(id+"F6.wireOp",EDGE,"E65.MirrorCS")])],"isStart":false})});
            var sketch = newSketch(context, id + "F16", { "sketchPlane" : qUnion([Q0])});
            skLineSegment(sketch, "E77.bottom", {"start": v(-17.8, 17) * mm, "end": v(16.2, 17) * mm});
            skLineSegment(sketch, "E77.top", {"start": v(-17.8, -17) * mm, "end": v(16.2, -17) * mm});
            skLineSegment(sketch, "E77.left", {"start": v(-18.8, 16) * mm, "end": v(-18.8, -16) * mm});
            skLineSegment(sketch, "E77.right", {"start": v(17.2, 16) * mm, "end": v(17.2, -16) * mm});
            skLineSegment(sketch, "E78.0.0", {"start": v(32.5, 22.5) * mm, "end": v(-32.5, 22.5) * mm});
            skLineSegment(sketch, "E78.0.1", {"start": v(-32.5, 22.5) * mm, "end": v(-32.5, -22.5) * mm});
            skLineSegment(sketch, "E78.0.2", {"start": v(-32.5, -22.5) * mm, "end": v(32.5, -22.5) * mm});
            skLineSegment(sketch, "E78.0.3", {"start": v(32.5, -22.5) * mm, "end": v(32.5, 22.5) * mm});
            skPoint(sketch, "E79.visualSharp", {"position": v(-18.8, 17) * mm});
            skArc(sketch, "E79.filletArc", {"start": v(-17.8, 17) * mm, "mid": v(-18.5, 16.7) * mm, "end": v(-18.8, 16) * mm});
            skPoint(sketch, "E80.visualSharp", {"position": v(17.2, 17) * mm});
            skArc(sketch, "E80.filletArc", {"start": v(17.2, 16) * mm, "mid": v(16.9, 16.7) * mm, "end": v(16.2, 17) * mm});
            skPoint(sketch, "E81.visualSharp", {"position": v(17.2, -17) * mm});
            skArc(sketch, "E81.filletArc", {"start": v(16.2, -17) * mm, "mid": v(16.9, -16.7) * mm, "end": v(17.2, -16) * mm});
            skPoint(sketch, "E82.visualSharp", {"position": v(-18.8, -17) * mm});
            skArc(sketch, "E82.filletArc", {"start": v(-18.8, -16) * mm, "mid": v(-18.5, -16.7) * mm, "end": v(-17.8, -17) * mm});
            skLineSegment(sketch, "E83", {"start": v(-18.8, 0) * mm, "end": v(17.2, 0) * mm, "construction": true});
            skPoint(sketch, "E84", {"position": v(-0.8, 0) * mm});
            skSolve(sketch);
        }
        {
            var Q0;
            Q0=makeQuery(id+"F16.imprint","IMPRINT",FACE,{"disambiguationData":[TD([[makeQuery(id+"F16.imprint","IMPRINT",EDGE,{"derivedFrom":sQuery(id+"F16.wireOp",EDGE,"E77.bottom")}),1.0]])]});
            extrude(context, id + "F17", {"entities" : qUnion([Q0]), "operationType" : NewBodyOperationType.REMOVE, "oppositeDirection" : true, "depth" : 1 * mm});
        }
        {
            var Q0;
            Q0=makeQuery(id+"F1.opExtrude","CAP_FACE",FACE,{"disambiguationData":[OSD([sQuery(id+"F0.wireOp",EDGE,"E0.bottom"),sQuery(id+"F0.wireOp",EDGE,"E0.top"),sQuery(id+"F0.wireOp",EDGE,"E0.left"),sQuery(id+"F0.wireOp",EDGE,"E0.right")])],"isStart":true});
            var sketch = newSketch(context, id + "F18", { "sketchPlane" : qUnion([Q0])});
            skLineSegment(sketch, "E85.bottom", {"start": v(-32.5, 22.5) * mm, "end": v(-31.5, 22.5) * mm});
            skLineSegment(sketch, "E85.top", {"start": v(-32.5, -22.5) * mm, "end": v(-31.5, -22.5) * mm});
            skLineSegment(sketch, "E85.left", {"start": v(-32.5, 22.5) * mm, "end": v(-32.5, -22.5) * mm});
            skLineSegment(sketch, "E85.right", {"start": v(-31.5, 22.5) * mm, "end": v(-31.5, -22.5) * mm});
            skCircle(sketch, "E86", {"center": v(-29, 0) * mm, "radius": 2.5 * mm});
            skLineSegment(sketch, "E87.bottom", {"start": v(-24.3, 18) * mm, "end": v(22.7, 18) * mm});
            skLineSegment(sketch, "E87.top", {"start": v(-24.3, -18) * mm, "end": v(22.7, -18) * mm});
            skLineSegment(sketch, "E87.left", {"start": v(-26.3, 16) * mm, "end": v(-26.3, -16) * mm});
            skLineSegment(sketch, "E87.right", {"start": v(24.7, 16) * mm, "end": v(24.7, -16) * mm});
            skCircle(sketch, "E88", {"center": v(29, 0) * mm, "radius": 2.5 * mm});
            skPoint(sketch, "E89.visualSharp", {"position": v(-26.3, 18) * mm});
            skArc(sketch, "E89.filletArc", {"start": v(-24.3, 18) * mm, "mid": v(-25.71, 17.41) * mm, "end": v(-26.3, 16) * mm});
            skPoint(sketch, "E90.visualSharp", {"position": v(24.7, 18) * mm});
            skArc(sketch, "E90.filletArc", {"start": v(24.7, 16) * mm, "mid": v(24.11, 17.41) * mm, "end": v(22.7, 18) * mm});
            skPoint(sketch, "E91.visualSharp", {"position": v(24.7, -18) * mm});
            skArc(sketch, "E91.filletArc", {"start": v(22.7, -18) * mm, "mid": v(24.11, -17.41) * mm, "end": v(24.7, -16) * mm});
            skPoint(sketch, "E92.visualSharp", {"position": v(-26.3, -18) * mm});
            skArc(sketch, "E92.filletArc", {"start": v(-26.3, -16) * mm, "mid": v(-25.71, -17.41) * mm, "end": v(-24.3, -18) * mm});
            skLineSegment(sketch, "E93.1.0.0", {"start": v(-28.45, 22.5) * mm, "end": v(-28.45, -22.5) * mm});
            skLineSegment(sketch, "E93.1.0.1", {"start": v(-29.45, 22.5) * mm, "end": v(-29.45, -22.5) * mm});
            skLineSegment(sketch, "E93.1.0.2", {"start": v(-29.45, -22.5) * mm, "end": v(-28.45, -22.5) * mm});
            skLineSegment(sketch, "E93.1.0.3", {"start": v(-29.45, 22.5) * mm, "end": v(-28.45, 22.5) * mm});
            skLineSegment(sketch, "E93.2.0.0", {"start": v(-25.4, 22.5) * mm, "end": v(-25.4, -22.5) * mm});
            skLineSegment(sketch, "E93.2.0.1", {"start": v(-26.4, 22.5) * mm, "end": v(-26.4, -22.5) * mm});
            skLineSegment(sketch, "E93.2.0.2", {"start": v(-26.4, -22.5) * mm, "end": v(-25.4, -22.5) * mm});
            skLineSegment(sketch, "E93.2.0.3", {"start": v(-26.4, 22.5) * mm, "end": v(-25.4, 22.5) * mm});
            skLineSegment(sketch, "E93.3.0.0", {"start": v(-22.36, 22.5) * mm, "end": v(-22.36, -22.5) * mm});
            skLineSegment(sketch, "E93.3.0.1", {"start": v(-23.36, 22.5) * mm, "end": v(-23.36, -22.5) * mm});
            skLineSegment(sketch, "E93.3.0.2", {"start": v(-23.36, -22.5) * mm, "end": v(-22.36, -22.5) * mm});
            skLineSegment(sketch, "E93.3.0.3", {"start": v(-23.36, 22.5) * mm, "end": v(-22.36, 22.5) * mm});
            skLineSegment(sketch, "E93.4.0.0", {"start": v(-19.3, 22.5) * mm, "end": v(-19.3, -22.5) * mm});
            skLineSegment(sketch, "E93.4.0.1", {"start": v(-20.3, 22.5) * mm, "end": v(-20.3, -22.5) * mm});
            skLineSegment(sketch, "E93.4.0.2", {"start": v(-20.3, -22.5) * mm, "end": v(-19.3, -22.5) * mm});
            skLineSegment(sketch, "E93.4.0.3", {"start": v(-20.3, 22.5) * mm, "end": v(-19.3, 22.5) * mm});
            skLineSegment(sketch, "E93.5.0.0", {"start": v(-16.26, 22.5) * mm, "end": v(-16.26, -22.5) * mm});
            skLineSegment(sketch, "E93.5.0.1", {"start": v(-17.26, 22.5) * mm, "end": v(-17.26, -22.5) * mm});
            skLineSegment(sketch, "E93.5.0.2", {"start": v(-17.26, -22.5) * mm, "end": v(-16.26, -22.5) * mm});
            skLineSegment(sketch, "E93.5.0.3", {"start": v(-17.26, 22.5) * mm, "end": v(-16.26, 22.5) * mm});
            skLineSegment(sketch, "E93.6.0.0", {"start": v(-13.21, 22.5) * mm, "end": v(-13.21, -22.5) * mm});
            skLineSegment(sketch, "E93.6.0.1", {"start": v(-14.21, 22.5) * mm, "end": v(-14.21, -22.5) * mm});
            skLineSegment(sketch, "E93.6.0.2", {"start": v(-14.21, -22.5) * mm, "end": v(-13.21, -22.5) * mm});
            skLineSegment(sketch, "E93.6.0.3", {"start": v(-14.21, 22.5) * mm, "end": v(-13.21, 22.5) * mm});
            skLineSegment(sketch, "E93.7.0.0", {"start": v(-10.17, 22.5) * mm, "end": v(-10.17, -22.5) * mm});
            skLineSegment(sketch, "E93.7.0.1", {"start": v(-11.17, 22.5) * mm, "end": v(-11.17, -22.5) * mm});
            skLineSegment(sketch, "E93.7.0.2", {"start": v(-11.17, -22.5) * mm, "end": v(-10.17, -22.5) * mm});
            skLineSegment(sketch, "E93.7.0.3", {"start": v(-11.17, 22.5) * mm, "end": v(-10.17, 22.5) * mm});
            skLineSegment(sketch, "E93.8.0.0", {"start": v(-7.12, 22.5) * mm, "end": v(-7.12, -22.5) * mm});
            skLineSegment(sketch, "E93.8.0.1", {"start": v(-8.12, 22.5) * mm, "end": v(-8.12, -22.5) * mm});
            skLineSegment(sketch, "E93.8.0.2", {"start": v(-8.12, -22.5) * mm, "end": v(-7.12, -22.5) * mm});
            skLineSegment(sketch, "E93.8.0.3", {"start": v(-8.12, 22.5) * mm, "end": v(-7.12, 22.5) * mm});
            skLineSegment(sketch, "E93.9.0.0", {"start": v(-4.07, 22.5) * mm, "end": v(-4.07, -22.5) * mm});
            skLineSegment(sketch, "E93.9.0.1", {"start": v(-5.07, 22.5) * mm, "end": v(-5.07, -22.5) * mm});
            skLineSegment(sketch, "E93.9.0.2", {"start": v(-5.07, -22.5) * mm, "end": v(-4.07, -22.5) * mm});
            skLineSegment(sketch, "E93.9.0.3", {"start": v(-5.07, 22.5) * mm, "end": v(-4.07, 22.5) * mm});
            skLineSegment(sketch, "E93.10.0.0", {"start": v(-1.02, 22.5) * mm, "end": v(-1.02, -22.5) * mm});
            skLineSegment(sketch, "E93.10.0.1", {"start": v(-2.02, 22.5) * mm, "end": v(-2.02, -22.5) * mm});
            skLineSegment(sketch, "E93.10.0.2", {"start": v(-2.02, -22.5) * mm, "end": v(-1.02, -22.5) * mm});
            skLineSegment(sketch, "E93.10.0.3", {"start": v(-2.02, 22.5) * mm, "end": v(-1.02, 22.5) * mm});
            skLineSegment(sketch, "E93.11.0.0", {"start": v(2.02, 22.5) * mm, "end": v(2.02, -22.5) * mm});
            skLineSegment(sketch, "E93.11.0.1", {"start": v(1.02, 22.5) * mm, "end": v(1.02, -22.5) * mm});
            skLineSegment(sketch, "E93.11.0.2", {"start": v(1.02, -22.5) * mm, "end": v(2.02, -22.5) * mm});
            skLineSegment(sketch, "E93.11.0.3", {"start": v(1.02, 22.5) * mm, "end": v(2.02, 22.5) * mm});
            skLineSegment(sketch, "E93.12.0.0", {"start": v(5.07, 22.5) * mm, "end": v(5.07, -22.5) * mm});
            skLineSegment(sketch, "E93.12.0.1", {"start": v(4.07, 22.5) * mm, "end": v(4.07, -22.5) * mm});
            skLineSegment(sketch, "E93.12.0.2", {"start": v(4.07, -22.5) * mm, "end": v(5.07, -22.5) * mm});
            skLineSegment(sketch, "E93.12.0.3", {"start": v(4.07, 22.5) * mm, "end": v(5.07, 22.5) * mm});
            skLineSegment(sketch, "E93.13.0.0", {"start": v(8.12, 22.5) * mm, "end": v(8.12, -22.5) * mm});
            skLineSegment(sketch, "E93.13.0.1", {"start": v(7.12, 22.5) * mm, "end": v(7.12, -22.5) * mm});
            skLineSegment(sketch, "E93.13.0.2", {"start": v(7.12, -22.5) * mm, "end": v(8.12, -22.5) * mm});
            skLineSegment(sketch, "E93.13.0.3", {"start": v(7.12, 22.5) * mm, "end": v(8.12, 22.5) * mm});
            skLineSegment(sketch, "E93.14.0.0", {"start": v(11.17, 22.5) * mm, "end": v(11.17, -22.5) * mm});
            skLineSegment(sketch, "E93.14.0.1", {"start": v(10.17, 22.5) * mm, "end": v(10.17, -22.5) * mm});
            skLineSegment(sketch, "E93.14.0.2", {"start": v(10.17, -22.5) * mm, "end": v(11.17, -22.5) * mm});
            skLineSegment(sketch, "E93.14.0.3", {"start": v(10.17, 22.5) * mm, "end": v(11.17, 22.5) * mm});
            skLineSegment(sketch, "E93.15.0.0", {"start": v(14.21, 22.5) * mm, "end": v(14.21, -22.5) * mm});
            skLineSegment(sketch, "E93.15.0.1", {"start": v(13.21, 22.5) * mm, "end": v(13.21, -22.5) * mm});
            skLineSegment(sketch, "E93.15.0.2", {"start": v(13.21, -22.5) * mm, "end": v(14.21, -22.5) * mm});
            skLineSegment(sketch, "E93.15.0.3", {"start": v(13.21, 22.5) * mm, "end": v(14.21, 22.5) * mm});
            skLineSegment(sketch, "E93.16.0.0", {"start": v(17.26, 22.5) * mm, "end": v(17.26, -22.5) * mm});
            skLineSegment(sketch, "E93.16.0.1", {"start": v(16.26, 22.5) * mm, "end": v(16.26, -22.5) * mm});
            skLineSegment(sketch, "E93.16.0.2", {"start": v(16.26, -22.5) * mm, "end": v(17.26, -22.5) * mm});
            skLineSegment(sketch, "E93.16.0.3", {"start": v(16.26, 22.5) * mm, "end": v(17.26, 22.5) * mm});
            skLineSegment(sketch, "E93.17.0.0", {"start": v(20.3, 22.5) * mm, "end": v(20.3, -22.5) * mm});
            skLineSegment(sketch, "E93.17.0.1", {"start": v(19.3, 22.5) * mm, "end": v(19.3, -22.5) * mm});
            skLineSegment(sketch, "E93.17.0.2", {"start": v(19.3, -22.5) * mm, "end": v(20.3, -22.5) * mm});
            skLineSegment(sketch, "E93.17.0.3", {"start": v(19.3, 22.5) * mm, "end": v(20.3, 22.5) * mm});
            skLineSegment(sketch, "E93.18.0.0", {"start": v(23.36, 22.5) * mm, "end": v(23.36, -22.5) * mm});
            skLineSegment(sketch, "E93.18.0.1", {"start": v(22.36, 22.5) * mm, "end": v(22.36, -22.5) * mm});
            skLineSegment(sketch, "E93.18.0.2", {"start": v(22.36, -22.5) * mm, "end": v(23.36, -22.5) * mm});
            skLineSegment(sketch, "E93.18.0.3", {"start": v(22.36, 22.5) * mm, "end": v(23.36, 22.5) * mm});
            skLineSegment(sketch, "E93.19.0.0", {"start": v(26.4, 22.5) * mm, "end": v(26.4, -22.5) * mm});
            skLineSegment(sketch, "E93.19.0.1", {"start": v(25.4, 22.5) * mm, "end": v(25.4, -22.5) * mm});
            skLineSegment(sketch, "E93.19.0.2", {"start": v(25.4, -22.5) * mm, "end": v(26.4, -22.5) * mm});
            skLineSegment(sketch, "E93.19.0.3", {"start": v(25.4, 22.5) * mm, "end": v(26.4, 22.5) * mm});
            skLineSegment(sketch, "E93.20.0.0", {"start": v(29.45, 22.5) * mm, "end": v(29.45, -22.5) * mm});
            skLineSegment(sketch, "E93.20.0.1", {"start": v(28.45, 22.5) * mm, "end": v(28.45, -22.5) * mm});
            skLineSegment(sketch, "E93.20.0.2", {"start": v(28.45, -22.5) * mm, "end": v(29.45, -22.5) * mm});
            skLineSegment(sketch, "E93.20.0.3", {"start": v(28.45, 22.5) * mm, "end": v(29.45, 22.5) * mm});
            skLineSegment(sketch, "E93.21.0.0", {"start": v(32.5, 22.5) * mm, "end": v(32.5, -22.5) * mm});
            skLineSegment(sketch, "E93.21.0.1", {"start": v(31.5, 22.5) * mm, "end": v(31.5, -22.5) * mm});
            skLineSegment(sketch, "E93.21.0.2", {"start": v(31.5, -22.5) * mm, "end": v(32.5, -22.5) * mm});
            skLineSegment(sketch, "E93.21.0.3", {"start": v(31.5, 22.5) * mm, "end": v(32.5, 22.5) * mm});
            skLineSegment(sketch, "E93.direction1", {"start": v(-31.5, -22.5) * mm, "end": v(-28.45, -22.5) * mm, "construction": true});
            skSolve(sketch);
        }
        {
            var Q0;
            {var subQ1=sQuery(id+"F18.wireOp",EDGE,"E85.bottom");Q0=makeQuery(id+"F18.imprint","IMPRINT",FACE,{"disambiguationData":[TD([[makeQuery(id+"F18.imprint","IMPRINT",EDGE,{"derivedFrom":subQ1}),1.0]])]});}
            var Q1;
            {var subQ5=sQuery(id+"F18.wireOp",EDGE,"E93.1.0.2");Q1=makeQuery(id+"F18.imprint","IMPRINT",FACE,{"disambiguationData":[TD([[makeQuery(id+"F18.imprint","IMPRINT",EDGE,{"derivedFrom":subQ5}),-1.0]])]});}
            var Q2;
            {var subQ5=sQuery(id+"F18.wireOp",EDGE,"E93.1.0.3");Q2=makeQuery(id+"F18.imprint","IMPRINT",FACE,{"disambiguationData":[TD([[makeQuery(id+"F18.imprint","IMPRINT",EDGE,{"derivedFrom":subQ5}),1.0]])]});}
            var Q3;
            {var subQ1=sQuery(id+"F18.wireOp",EDGE,"E87.left");Q3=makeQuery(id+"F18.imprint","IMPRINT",FACE,{"disambiguationData":[TD([[makeQuery(id+"F18.imprint","IMPRINT",EDGE,{"derivedFrom":subQ1}),-1.0]])]});}
            var Q4;
            {var subQ5=sQuery(id+"F18.wireOp",EDGE,"E93.3.0.2");Q4=makeQuery(id+"F18.imprint","IMPRINT",FACE,{"disambiguationData":[TD([[makeQuery(id+"F18.imprint","IMPRINT",EDGE,{"derivedFrom":subQ5}),-1.0]])]});}
            var Q5;
            {var subQ5=sQuery(id+"F18.wireOp",EDGE,"E93.4.0.2");Q5=makeQuery(id+"F18.imprint","IMPRINT",FACE,{"disambiguationData":[TD([[makeQuery(id+"F18.imprint","IMPRINT",EDGE,{"derivedFrom":subQ5}),-1.0]])]});}
            var Q6;
            {var subQ5=sQuery(id+"F18.wireOp",EDGE,"E93.5.0.2");Q6=makeQuery(id+"F18.imprint","IMPRINT",FACE,{"disambiguationData":[TD([[makeQuery(id+"F18.imprint","IMPRINT",EDGE,{"derivedFrom":subQ5}),-1.0]])]});}
            var Q7;
            {var subQ5=sQuery(id+"F18.wireOp",EDGE,"E93.6.0.2");Q7=makeQuery(id+"F18.imprint","IMPRINT",FACE,{"disambiguationData":[TD([[makeQuery(id+"F18.imprint","IMPRINT",EDGE,{"derivedFrom":subQ5}),-1.0]])]});}
            var Q8;
            {var subQ5=sQuery(id+"F18.wireOp",EDGE,"E93.7.0.2");Q8=makeQuery(id+"F18.imprint","IMPRINT",FACE,{"disambiguationData":[TD([[makeQuery(id+"F18.imprint","IMPRINT",EDGE,{"derivedFrom":subQ5}),-1.0]])]});}
            var Q9;
            {var subQ5=sQuery(id+"F18.wireOp",EDGE,"E93.8.0.2");Q9=makeQuery(id+"F18.imprint","IMPRINT",FACE,{"disambiguationData":[TD([[makeQuery(id+"F18.imprint","IMPRINT",EDGE,{"derivedFrom":subQ5}),-1.0]])]});}
            var Q10;
            {var subQ5=sQuery(id+"F18.wireOp",EDGE,"E93.9.0.2");Q10=makeQuery(id+"F18.imprint","IMPRINT",FACE,{"disambiguationData":[TD([[makeQuery(id+"F18.imprint","IMPRINT",EDGE,{"derivedFrom":subQ5}),-1.0]])]});}
            var Q11;
            {var subQ5=sQuery(id+"F18.wireOp",EDGE,"E93.10.0.2");Q11=makeQuery(id+"F18.imprint","IMPRINT",FACE,{"disambiguationData":[TD([[makeQuery(id+"F18.imprint","IMPRINT",EDGE,{"derivedFrom":subQ5}),-1.0]])]});}
            var Q12;
            {var subQ5=sQuery(id+"F18.wireOp",EDGE,"E93.11.0.2");Q12=makeQuery(id+"F18.imprint","IMPRINT",FACE,{"disambiguationData":[TD([[makeQuery(id+"F18.imprint","IMPRINT",EDGE,{"derivedFrom":subQ5}),-1.0]])]});}
            var Q13;
            {var subQ5=sQuery(id+"F18.wireOp",EDGE,"E93.12.0.2");Q13=makeQuery(id+"F18.imprint","IMPRINT",FACE,{"disambiguationData":[TD([[makeQuery(id+"F18.imprint","IMPRINT",EDGE,{"derivedFrom":subQ5}),-1.0]])]});}
            var Q14;
            {var subQ5=sQuery(id+"F18.wireOp",EDGE,"E93.13.0.2");Q14=makeQuery(id+"F18.imprint","IMPRINT",FACE,{"disambiguationData":[TD([[makeQuery(id+"F18.imprint","IMPRINT",EDGE,{"derivedFrom":subQ5}),-1.0]])]});}
            var Q15;
            {var subQ5=sQuery(id+"F18.wireOp",EDGE,"E93.14.0.2");Q15=makeQuery(id+"F18.imprint","IMPRINT",FACE,{"disambiguationData":[TD([[makeQuery(id+"F18.imprint","IMPRINT",EDGE,{"derivedFrom":subQ5}),-1.0]])]});}
            var Q16;
            {var subQ5=sQuery(id+"F18.wireOp",EDGE,"E93.15.0.2");Q16=makeQuery(id+"F18.imprint","IMPRINT",FACE,{"disambiguationData":[TD([[makeQuery(id+"F18.imprint","IMPRINT",EDGE,{"derivedFrom":subQ5}),-1.0]])]});}
            var Q17;
            {var subQ5=sQuery(id+"F18.wireOp",EDGE,"E93.16.0.2");Q17=makeQuery(id+"F18.imprint","IMPRINT",FACE,{"disambiguationData":[TD([[makeQuery(id+"F18.imprint","IMPRINT",EDGE,{"derivedFrom":subQ5}),-1.0]])]});}
            var Q18;
            {var subQ5=sQuery(id+"F18.wireOp",EDGE,"E93.17.0.2");Q18=makeQuery(id+"F18.imprint","IMPRINT",FACE,{"disambiguationData":[TD([[makeQuery(id+"F18.imprint","IMPRINT",EDGE,{"derivedFrom":subQ5}),-1.0]])]});}
            var Q19;
            {var subQ5=sQuery(id+"F18.wireOp",EDGE,"E93.18.0.2");Q19=makeQuery(id+"F18.imprint","IMPRINT",FACE,{"disambiguationData":[TD([[makeQuery(id+"F18.imprint","IMPRINT",EDGE,{"derivedFrom":subQ5}),-1.0]])]});}
            var Q20;
            {var subQ5=sQuery(id+"F18.wireOp",EDGE,"E93.20.0.2");Q20=makeQuery(id+"F18.imprint","IMPRINT",FACE,{"disambiguationData":[TD([[makeQuery(id+"F18.imprint","IMPRINT",EDGE,{"derivedFrom":subQ5}),-1.0]])]});}
            var Q21;
            {var subQ5=sQuery(id+"F18.wireOp",EDGE,"E93.21.0.2");Q21=makeQuery(id+"F18.imprint","IMPRINT",FACE,{"disambiguationData":[TD([[makeQuery(id+"F18.imprint","IMPRINT",EDGE,{"derivedFrom":subQ5}),-1.0]])]});}
            var Q22;
            {var subQ5=sQuery(id+"F18.wireOp",EDGE,"E93.21.0.3");Q22=makeQuery(id+"F18.imprint","IMPRINT",FACE,{"disambiguationData":[TD([[makeQuery(id+"F18.imprint","IMPRINT",EDGE,{"derivedFrom":subQ5}),1.0]])]});}
            var Q23;
            {var subQ5=sQuery(id+"F18.wireOp",EDGE,"E93.20.0.3");Q23=makeQuery(id+"F18.imprint","IMPRINT",FACE,{"disambiguationData":[TD([[makeQuery(id+"F18.imprint","IMPRINT",EDGE,{"derivedFrom":subQ5}),1.0]])]});}
            var Q24;
            {var subQ5=sQuery(id+"F18.wireOp",EDGE,"E93.18.0.3");Q24=makeQuery(id+"F18.imprint","IMPRINT",FACE,{"disambiguationData":[TD([[makeQuery(id+"F18.imprint","IMPRINT",EDGE,{"derivedFrom":subQ5}),1.0]])]});}
            var Q25;
            {var subQ5=sQuery(id+"F18.wireOp",EDGE,"E93.17.0.3");Q25=makeQuery(id+"F18.imprint","IMPRINT",FACE,{"disambiguationData":[TD([[makeQuery(id+"F18.imprint","IMPRINT",EDGE,{"derivedFrom":subQ5}),1.0]])]});}
            var Q26;
            {var subQ5=sQuery(id+"F18.wireOp",EDGE,"E93.16.0.3");Q26=makeQuery(id+"F18.imprint","IMPRINT",FACE,{"disambiguationData":[TD([[makeQuery(id+"F18.imprint","IMPRINT",EDGE,{"derivedFrom":subQ5}),1.0]])]});}
            var Q27;
            {var subQ5=sQuery(id+"F18.wireOp",EDGE,"E93.15.0.3");Q27=makeQuery(id+"F18.imprint","IMPRINT",FACE,{"disambiguationData":[TD([[makeQuery(id+"F18.imprint","IMPRINT",EDGE,{"derivedFrom":subQ5}),1.0]])]});}
            var Q28;
            {var subQ5=sQuery(id+"F18.wireOp",EDGE,"E93.14.0.3");Q28=makeQuery(id+"F18.imprint","IMPRINT",FACE,{"disambiguationData":[TD([[makeQuery(id+"F18.imprint","IMPRINT",EDGE,{"derivedFrom":subQ5}),1.0]])]});}
            var Q29;
            {var subQ5=sQuery(id+"F18.wireOp",EDGE,"E93.13.0.3");Q29=makeQuery(id+"F18.imprint","IMPRINT",FACE,{"disambiguationData":[TD([[makeQuery(id+"F18.imprint","IMPRINT",EDGE,{"derivedFrom":subQ5}),1.0]])]});}
            var Q30;
            {var subQ5=sQuery(id+"F18.wireOp",EDGE,"E93.12.0.3");Q30=makeQuery(id+"F18.imprint","IMPRINT",FACE,{"disambiguationData":[TD([[makeQuery(id+"F18.imprint","IMPRINT",EDGE,{"derivedFrom":subQ5}),1.0]])]});}
            var Q31;
            {var subQ5=sQuery(id+"F18.wireOp",EDGE,"E93.11.0.3");Q31=makeQuery(id+"F18.imprint","IMPRINT",FACE,{"disambiguationData":[TD([[makeQuery(id+"F18.imprint","IMPRINT",EDGE,{"derivedFrom":subQ5}),1.0]])]});}
            var Q32;
            {var subQ5=sQuery(id+"F18.wireOp",EDGE,"E93.10.0.3");Q32=makeQuery(id+"F18.imprint","IMPRINT",FACE,{"disambiguationData":[TD([[makeQuery(id+"F18.imprint","IMPRINT",EDGE,{"derivedFrom":subQ5}),1.0]])]});}
            var Q33;
            {var subQ5=sQuery(id+"F18.wireOp",EDGE,"E93.9.0.3");Q33=makeQuery(id+"F18.imprint","IMPRINT",FACE,{"disambiguationData":[TD([[makeQuery(id+"F18.imprint","IMPRINT",EDGE,{"derivedFrom":subQ5}),1.0]])]});}
            var Q34;
            {var subQ5=sQuery(id+"F18.wireOp",EDGE,"E93.8.0.3");Q34=makeQuery(id+"F18.imprint","IMPRINT",FACE,{"disambiguationData":[TD([[makeQuery(id+"F18.imprint","IMPRINT",EDGE,{"derivedFrom":subQ5}),1.0]])]});}
            var Q35;
            {var subQ5=sQuery(id+"F18.wireOp",EDGE,"E93.7.0.3");Q35=makeQuery(id+"F18.imprint","IMPRINT",FACE,{"disambiguationData":[TD([[makeQuery(id+"F18.imprint","IMPRINT",EDGE,{"derivedFrom":subQ5}),1.0]])]});}
            var Q36;
            {var subQ5=sQuery(id+"F18.wireOp",EDGE,"E93.6.0.3");Q36=makeQuery(id+"F18.imprint","IMPRINT",FACE,{"disambiguationData":[TD([[makeQuery(id+"F18.imprint","IMPRINT",EDGE,{"derivedFrom":subQ5}),1.0]])]});}
            var Q37;
            {var subQ5=sQuery(id+"F18.wireOp",EDGE,"E93.5.0.3");Q37=makeQuery(id+"F18.imprint","IMPRINT",FACE,{"disambiguationData":[TD([[makeQuery(id+"F18.imprint","IMPRINT",EDGE,{"derivedFrom":subQ5}),1.0]])]});}
            var Q38;
            {var subQ5=sQuery(id+"F18.wireOp",EDGE,"E93.4.0.3");Q38=makeQuery(id+"F18.imprint","IMPRINT",FACE,{"disambiguationData":[TD([[makeQuery(id+"F18.imprint","IMPRINT",EDGE,{"derivedFrom":subQ5}),1.0]])]});}
            var Q39;
            {var subQ5=sQuery(id+"F18.wireOp",EDGE,"E93.3.0.3");Q39=makeQuery(id+"F18.imprint","IMPRINT",FACE,{"disambiguationData":[TD([[makeQuery(id+"F18.imprint","IMPRINT",EDGE,{"derivedFrom":subQ5}),1.0]])]});}
            var Q40;
            Q40=makeQuery(id+"F18.imprint","IMPRINT",FACE,{"disambiguationData":[TD([[makeQuery(id+"F18.imprint","IMPRINT",EDGE,{"derivedFrom":sQuery(id+"F18.wireOp",EDGE,"E93.19.0.0")}),-1.0]])]});
            extrude(context, id + "F19", {"entities" : qUnion([Q0, Q1, Q2, Q3, Q4, Q5, Q6, Q7, Q8, Q9, Q10, Q11, Q12, Q13, Q14, Q15, Q16, Q17, Q18, Q19, Q20, Q21, Q22, Q23, Q24, Q25, Q26, Q27, Q28, Q29, Q30, Q31, Q32, Q33, Q34, Q35, Q36, Q37, Q38, Q39, Q40]), "operationType" : NewBodyOperationType.ADD, "depth" : 3 * mm});
        }
    });
